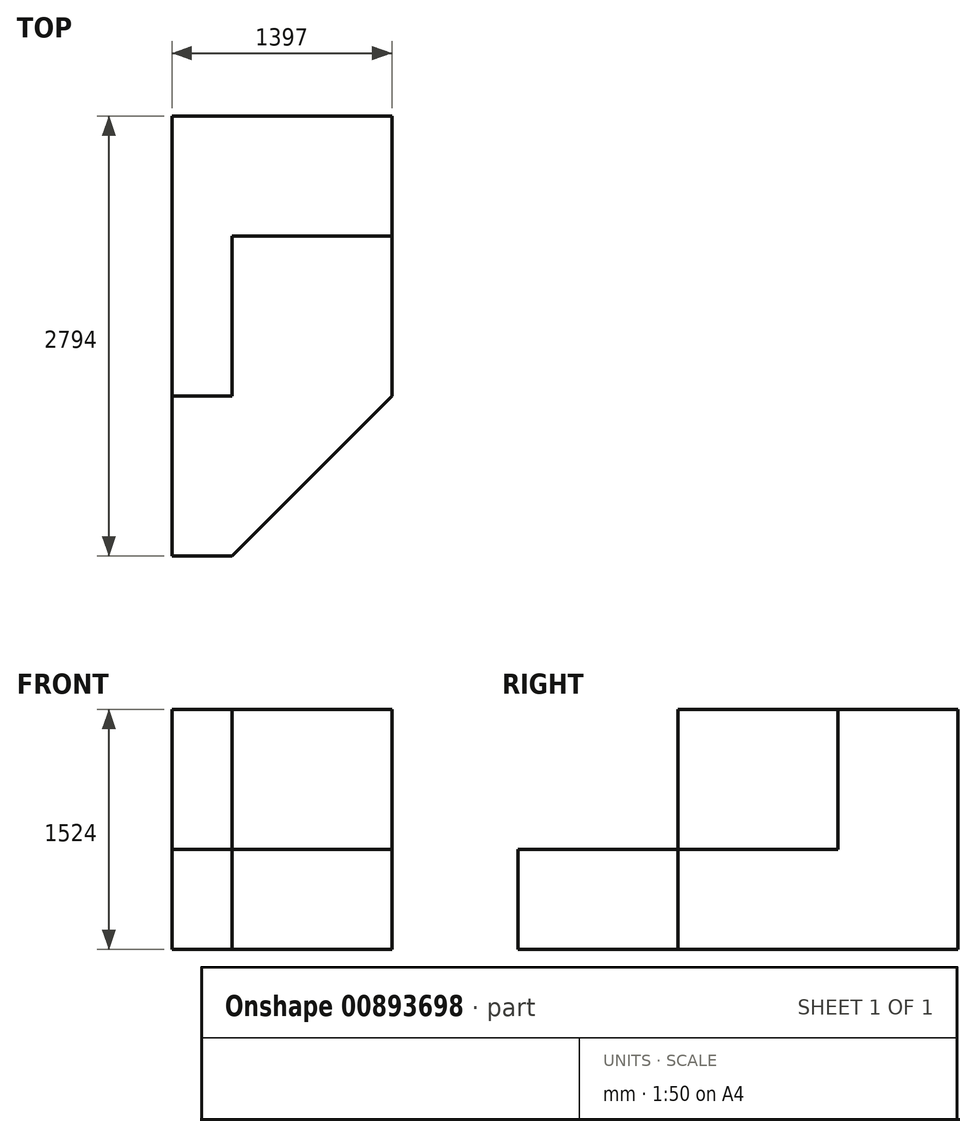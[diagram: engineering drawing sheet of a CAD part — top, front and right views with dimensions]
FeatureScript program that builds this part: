
annotation { "Feature Type Name" : "Feature", "Feature Type Description" : "" }
export const myFeature = defineFeature(function(context is Context, id is Id, definition is map)
    precondition{}
    {
        {
            var Q0;
            Q0=qCreatedBy(makeId("Top.planeOp"),FACE);
            var sketch = newSketch(context, id + "F0", { "sketchPlane" : qUnion([Q0])});
            skLineSegment(sketch, "E0", {"start": v(0, 1397) * mm, "end": v(-698.5, 1397) * mm});
            skLineSegment(sketch, "E1", {"start": v(-698.5, 1397) * mm, "end": v(-698.5, -1397) * mm});
            skLineSegment(sketch, "E2", {"start": v(-698.5, -1397) * mm, "end": v(-317.5, -1397) * mm});
            skLineSegment(sketch, "E3", {"start": v(-317.5, -1397) * mm, "end": v(698.5, -381) * mm});
            skLineSegment(sketch, "E4", {"start": v(698.5, -381) * mm, "end": v(698.5, 1397) * mm});
            skLineSegment(sketch, "E5", {"start": v(698.5, 1397) * mm, "end": v(0, 1397) * mm});
            skSolve(sketch);
        }
        {
            var Q0;
            Q0=makeQuery(id+"F0.imprint","IMPRINT",FACE,{"disambiguationData":[TD([[makeQuery(id+"F0.imprint","IMPRINT",EDGE,{"derivedFrom":sQuery(id+"F0.wireOp",EDGE,"E0")}),1.0]])]});
            extrude(context, id + "F1", {"entities" : qUnion([Q0]), "depth" : 635 * mm, "offsetDistance" : 25.4 * mm});
        }
        {
            var Q0;
            Q0=makeQuery(id+"F1.opExtrude","CAP_FACE",FACE,{"disambiguationData":[OSD([sQuery(id+"F0.wireOp",EDGE,"E0"),sQuery(id+"F0.wireOp",EDGE,"E1"),sQuery(id+"F0.wireOp",EDGE,"E2"),sQuery(id+"F0.wireOp",EDGE,"E3"),sQuery(id+"F0.wireOp",EDGE,"E4"),sQuery(id+"F0.wireOp",EDGE,"E5")])],"isStart":false});
            var sketch = newSketch(context, id + "F2", { "sketchPlane" : qUnion([Q0])});
            skLineSegment(sketch, "E6", {"start": v(-698.5, 1397) * mm, "end": v(-698.5, -381) * mm});
            skLineSegment(sketch, "E7", {"start": v(-698.5, -381) * mm, "end": v(-317.5, -381) * mm});
            skLineSegment(sketch, "E8", {"start": v(-317.5, -381) * mm, "end": v(-317.5, 635) * mm});
            skLineSegment(sketch, "E9", {"start": v(-317.5, 635) * mm, "end": v(698.5, 635) * mm});
            skLineSegment(sketch, "E10", {"start": v(698.5, 635) * mm, "end": v(698.5, 1397) * mm});
            skLineSegment(sketch, "E11", {"start": v(698.5, 1397) * mm, "end": v(-698.5, 1397) * mm});
            skSolve(sketch);
        }
        {
            var Q0;
            Q0=makeQuery(id+"F2.imprint","IMPRINT",FACE,{"disambiguationData":[TD([[makeQuery(id+"F2.imprint","IMPRINT",EDGE,{"derivedFrom":sQuery(id+"F2.wireOp",EDGE,"E6")}),1.0]])]});
            extrude(context, id + "F3", {"entities" : qUnion([Q0]), "operationType" : NewBodyOperationType.ADD, "depth" : 889 * mm, "offsetDistance" : 25.4 * mm});
        }
    });
